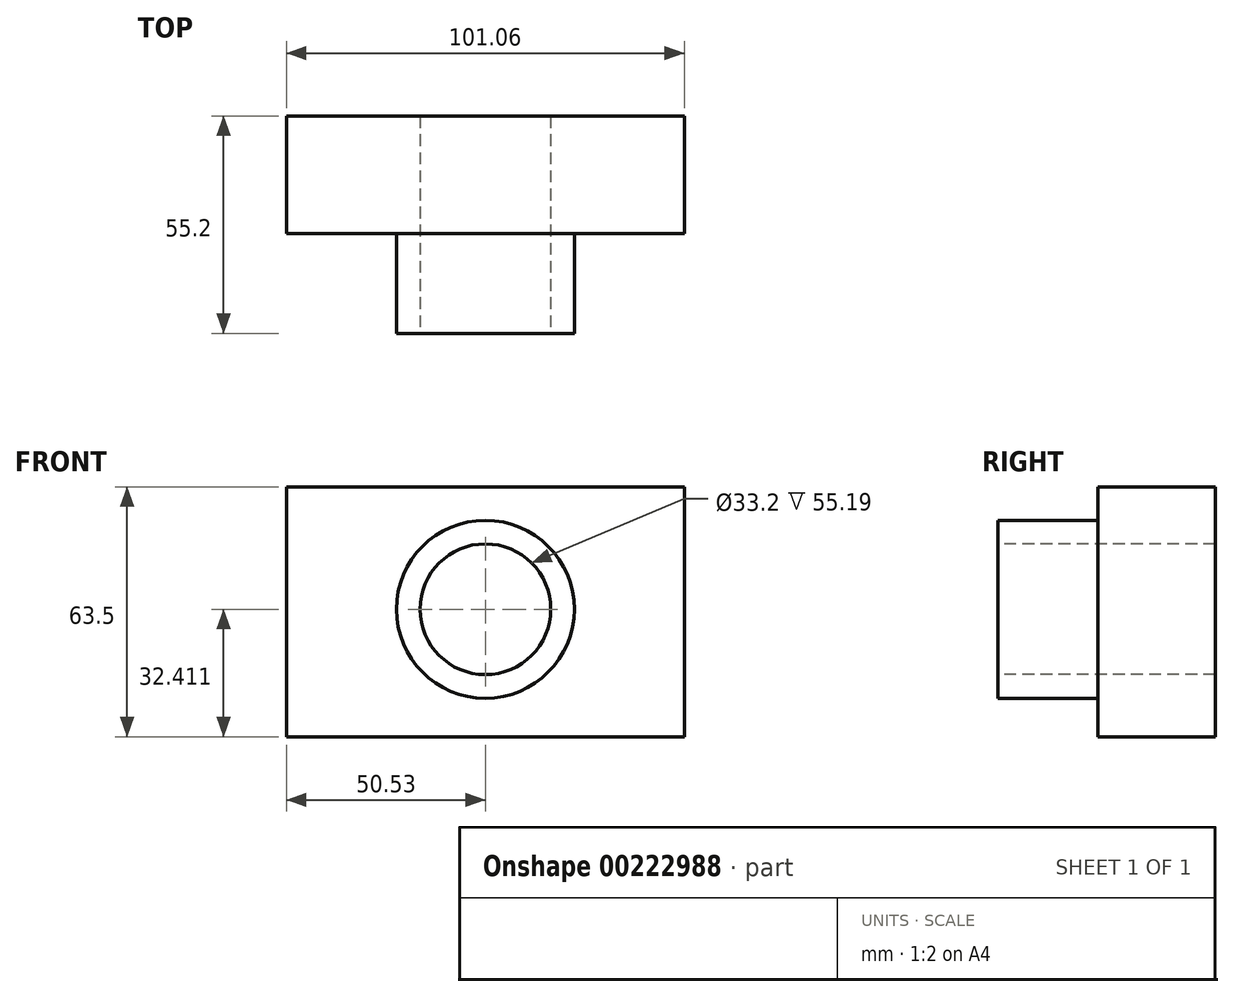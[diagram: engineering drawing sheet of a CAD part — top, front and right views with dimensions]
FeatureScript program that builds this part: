
annotation { "Feature Type Name" : "Feature", "Feature Type Description" : "" }
export const myFeature = defineFeature(function(context is Context, id is Id, definition is map)
    precondition{}
    {
        {
            var Q0;
            Q0=qCreatedBy(makeId("Top.planeOp"),FACE);
            var sketch = newSketch(context, id + "F0", { "sketchPlane" : qUnion([Q0])});
            skLineSegment(sketch, "E0.bottom", {"start": v(50.53, -14.9) * mm, "end": v(-50.53, -14.9) * mm});
            skLineSegment(sketch, "E0.top", {"start": v(50.53, 14.9) * mm, "end": v(-50.53, 14.9) * mm});
            skLineSegment(sketch, "E0.left", {"start": v(50.53, -14.9) * mm, "end": v(50.53, 14.9) * mm});
            skLineSegment(sketch, "E0.right", {"start": v(-50.53, -14.9) * mm, "end": v(-50.53, 14.9) * mm});
            skPoint(sketch, "E0.middle", {"position": v(0, 0) * mm});
            skSolve(sketch);
        }
        {
            var Q0;
            Q0 = qSketchRegion(id + "F0", true);
            extrude(context, id + "F1", {"entities" : qUnion([Q0]), "depth" : 63.5 * mm});
        }
        {
            var Q0;
            Q0=makeQuery(id+"F1.opExtrude","SWEPT_FACE",FACE,{"disambiguationData":[OSD([sQuery(id+"F0.wireOp",EDGE,"E0.bottom")])]});
            var sketch = newSketch(context, id + "F2", { "sketchPlane" : qUnion([Q0])});
            skCircle(sketch, "E1", {"center": v(0, 32.41) * mm, "radius": 22.6 * mm});
            skSolve(sketch);
        }
        {
            var Q0;
            Q0=makeQuery(id+"F2.imprint","IMPRINT",FACE,{"disambiguationData":[TD([[makeQuery(id+"F2.imprint","IMPRINT",EDGE,{"derivedFrom":sQuery(id+"F2.wireOp",EDGE,"E1")}),1.0]])]});
            extrude(context, id + "F3", {"entities" : qUnion([Q0]), "operationType" : NewBodyOperationType.ADD, "depth" : 25.4 * mm});
        }
        {
            var Q0;
            Q0=makeQuery(id+"F3.opExtrude","CAP_FACE",FACE,{"disambiguationData":[OSD([sQuery(id+"F2.wireOp",EDGE,"E1")])],"isStart":false});
            var sketch = newSketch(context, id + "F4", { "sketchPlane" : qUnion([Q0])});
            skCircle(sketch, "E2", {"center": v(0, 32.41) * mm, "radius": 16.6 * mm});
            skSolve(sketch);
        }
        {
            var Q0;
            Q0=makeQuery(id+"F4.imprint","IMPRINT",FACE,{"disambiguationData":[TD([[makeQuery(id+"F4.imprint","IMPRINT",EDGE,{"derivedFrom":sQuery(id+"F4.wireOp",EDGE,"E2")}),1.0]])]});
            extrude(context, id + "F5", {"entities" : qUnion([Q0]), "operationType" : NewBodyOperationType.REMOVE, "endBound" : BoundingType.THROUGH_ALL, "oppositeDirection" : true, "depth" : 25.4 * mm});
        }
    });
